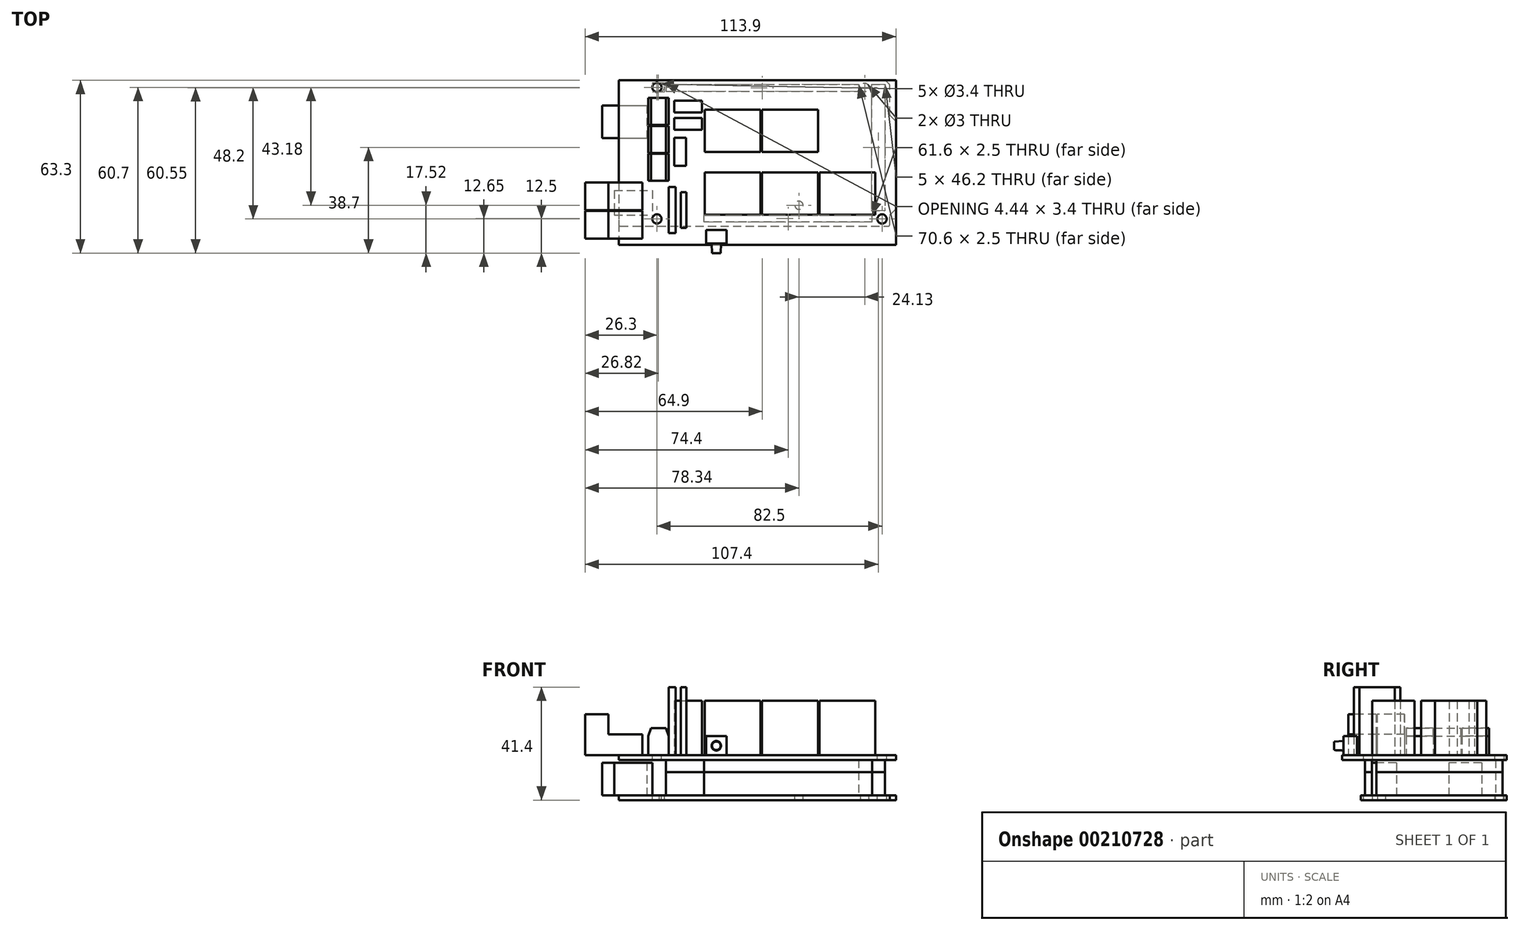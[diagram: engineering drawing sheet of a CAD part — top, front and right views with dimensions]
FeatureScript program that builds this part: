
annotation { "Feature Type Name" : "Feature", "Feature Type Description" : "" }
export const myFeature = defineFeature(function(context is Context, id is Id, definition is map)
    precondition{}
    {
        {
            var Q0;
            Q0=qCreatedBy(makeId("Top.planeOp"),FACE);
            var sketch = newSketch(context, id + "F0", { "sketchPlane" : qUnion([Q0])});
            skLineSegment(sketch, "E0.bottom", {"start": v(-50.8, 26.7) * mm, "end": v(50.8, 26.7) * mm, "construction": true});
            skLineSegment(sketch, "E0.top", {"start": v(-50.8, -26.7) * mm, "end": v(50.8, -26.7) * mm, "construction": true});
            skLineSegment(sketch, "E0.left", {"start": v(-50.8, 26.7) * mm, "end": v(-50.8, -26.7) * mm});
            skLineSegment(sketch, "E0.right", {"start": v(50.8, 26.7) * mm, "end": v(50.8, -26.7) * mm, "construction": true});
            skLineSegment(sketch, "E1", {"start": v(50.8, -26.7) * mm, "end": v(-50.8, 26.7) * mm, "construction": true});
            skLineSegment(sketch, "E2", {"start": v(-50.8, -26.7) * mm, "end": v(48.5, -26.7) * mm});
            skLineSegment(sketch, "E3", {"start": v(48.5, -26.7) * mm, "end": v(48.5, -22.7) * mm});
            skLineSegment(sketch, "E4", {"start": v(48.5, -22.7) * mm, "end": v(50.8, -20.4) * mm});
            skLineSegment(sketch, "E5", {"start": v(50.8, -20.4) * mm, "end": v(50.8, 11.6) * mm});
            skLineSegment(sketch, "E6", {"start": v(50.8, 11.6) * mm, "end": v(48.5, 13.9) * mm});
            skLineSegment(sketch, "E7", {"start": v(48.5, 13.9) * mm, "end": v(48.5, 25.1) * mm});
            skLineSegment(sketch, "E8", {"start": v(48.5, 25.1) * mm, "end": v(46.9, 26.7) * mm});
            skLineSegment(sketch, "E9", {"start": v(46.9, 26.7) * mm, "end": v(-50.8, 26.7) * mm});
            skSolve(sketch);
        }
        {
            var Q0;
            Q0=makeQuery(id+"F0.imprint","IMPRINT",FACE,{"disambiguationData":[TD([[makeQuery(id+"F0.imprint","IMPRINT",EDGE,{"derivedFrom":sQuery(id+"F0.wireOp",EDGE,"E0.left")}),1.0]])]});
            extrude(context, id + "F1", {"entities" : qUnion([Q0]), "depth" : 1.7 * mm});
        }
        {
            var Q0;
            Q0=makeQuery(id+"F1.opExtrude","CAP_FACE",FACE,{"disambiguationData":[OSD([sQuery(id+"F0.wireOp",EDGE,"E0.left"),sQuery(id+"F0.wireOp",EDGE,"E2"),sQuery(id+"F0.wireOp",EDGE,"E3"),sQuery(id+"F0.wireOp",EDGE,"E4"),sQuery(id+"F0.wireOp",EDGE,"E5"),sQuery(id+"F0.wireOp",EDGE,"E6"),sQuery(id+"F0.wireOp",EDGE,"E7"),sQuery(id+"F0.wireOp",EDGE,"E8"),sQuery(id+"F0.wireOp",EDGE,"E9")])],"isStart":false});
            var sketch = newSketch(context, id + "F2", { "sketchPlane" : qUnion([Q0])});
            skPoint(sketch, "E10", {"position": v(-35.56, 24.1) * mm});
            skPoint(sketch, "E11", {"position": v(39.37, 24.1) * mm});
            skPoint(sketch, "E12", {"position": v(15.24, -19.08) * mm});
            skPoint(sketch, "E13", {"position": v(-36.83, -24.16) * mm});
            skPoint(sketch, "E14", {"position": v(45.72, -24.16) * mm});
            skSolve(sketch);
        }
        {
            var Q0;
            Q0=sQuery(id+"F2.wireOp",VERTEX,"E10");
            var Q1;
            Q1=sQuery(id+"F2.wireOp",VERTEX,"E11");
            var Q2;
            Q2=sQuery(id+"F2.wireOp",VERTEX,"E12");
            var Q3;
            Q3=sQuery(id+"F2.wireOp",VERTEX,"E14");
            var Q4;
            Q4=sQuery(id+"F2.wireOp",VERTEX,"E13");
            var Q5;
            Q5=makeQuery(id+"F1.opExtrude","SWEPT_BODY",BODY,{"disambiguationData":[OSD([sQuery(id+"F0.wireOp",EDGE,"E0.left"),sQuery(id+"F0.wireOp",EDGE,"E2"),sQuery(id+"F0.wireOp",EDGE,"E3"),sQuery(id+"F0.wireOp",EDGE,"E4"),sQuery(id+"F0.wireOp",EDGE,"E5"),sQuery(id+"F0.wireOp",EDGE,"E6"),sQuery(id+"F0.wireOp",EDGE,"E7"),sQuery(id+"F0.wireOp",EDGE,"E8"),sQuery(id+"F0.wireOp",EDGE,"E9")])]});
            hole(context, id + "F3", {"style" : HoleStyle.SIMPLE, "endStyle" : HoleEndStyle.THROUGH, "holeDiameter" : 3 * mm, "locations" : qUnion([Q0, Q1, Q2, Q3, Q4]), "scope" : qUnion([Q5]), "isTappedThrough" : true});
        }
        {
            var Q0;
            Q0=makeQuery(id+"F1.opExtrude","SWEPT_EDGE",EDGE,{"disambiguationData":[OSD([sQuery(id+"F0.wireOp",EDGE,"E0.left"),sQuery(id+"F0.wireOp",EDGE,"E9")])]});
            var Q1;
            Q1=makeQuery(id+"F1.opExtrude","SWEPT_EDGE",EDGE,{"disambiguationData":[OSD([sQuery(id+"F0.wireOp",EDGE,"E0.left"),sQuery(id+"F0.wireOp",EDGE,"E2")])]});
            var Q2;
            Q2=makeQuery(id+"F1.opExtrude","SWEPT_EDGE",EDGE,{"disambiguationData":[OSD([sQuery(id+"F0.wireOp",EDGE,"E2"),sQuery(id+"F0.wireOp",EDGE,"E3")])]});
            var Q3;
            Q3=makeQuery(id+"F1.opExtrude","SWEPT_EDGE",EDGE,{"disambiguationData":[OSD([sQuery(id+"F0.wireOp",EDGE,"E3"),sQuery(id+"F0.wireOp",EDGE,"E4")])]});
            var Q4;
            Q4=makeQuery(id+"F1.opExtrude","SWEPT_EDGE",EDGE,{"disambiguationData":[OSD([sQuery(id+"F0.wireOp",EDGE,"E4"),sQuery(id+"F0.wireOp",EDGE,"E5")])]});
            var Q5;
            Q5=makeQuery(id+"F1.opExtrude","SWEPT_EDGE",EDGE,{"disambiguationData":[OSD([sQuery(id+"F0.wireOp",EDGE,"E5"),sQuery(id+"F0.wireOp",EDGE,"E6")])]});
            var Q6;
            Q6=makeQuery(id+"F1.opExtrude","SWEPT_EDGE",EDGE,{"disambiguationData":[OSD([sQuery(id+"F0.wireOp",EDGE,"E6"),sQuery(id+"F0.wireOp",EDGE,"E7")])]});
            var Q7;
            Q7=makeQuery(id+"F1.opExtrude","SWEPT_EDGE",EDGE,{"disambiguationData":[OSD([sQuery(id+"F0.wireOp",EDGE,"E7"),sQuery(id+"F0.wireOp",EDGE,"E8")])]});
            var Q8;
            Q8=makeQuery(id+"F1.opExtrude","SWEPT_EDGE",EDGE,{"disambiguationData":[OSD([sQuery(id+"F0.wireOp",EDGE,"E8"),sQuery(id+"F0.wireOp",EDGE,"E9")])]});
            fillet(context, id + "F4", {"entities" : qUnion([Q0, Q1, Q2, Q3, Q4, Q5, Q6, Q7, Q8]), "radius" : .5 * mm, "tangentPropagation" : true, "allowEdgeOverflow" : false});
        }
        {
            var Q0;
            Q0=makeQuery(id+"F1.opExtrude","CAP_FACE",FACE,{"disambiguationData":[OSD([sQuery(id+"F0.wireOp",EDGE,"E0.left"),sQuery(id+"F0.wireOp",EDGE,"E2"),sQuery(id+"F0.wireOp",EDGE,"E3"),sQuery(id+"F0.wireOp",EDGE,"E4"),sQuery(id+"F0.wireOp",EDGE,"E5"),sQuery(id+"F0.wireOp",EDGE,"E6"),sQuery(id+"F0.wireOp",EDGE,"E7"),sQuery(id+"F0.wireOp",EDGE,"E8"),sQuery(id+"F0.wireOp",EDGE,"E9")])],"isStart":false});
            var sketch = newSketch(context, id + "F5", { "sketchPlane" : qUnion([Q0])});
            skLineSegment(sketch, "E15.bottom", {"start": v(-52.4, -13.7) * mm, "end": v(-38.4, -13.7) * mm});
            skLineSegment(sketch, "E15.top", {"start": v(-52.4, -22.7) * mm, "end": v(-38.4, -22.7) * mm});
            skLineSegment(sketch, "E15.left", {"start": v(-52.4, -13.7) * mm, "end": v(-52.4, -22.7) * mm});
            skLineSegment(sketch, "E15.right", {"start": v(-38.4, -13.7) * mm, "end": v(-38.4, -22.7) * mm});
            skLineSegment(sketch, "E16.bottom", {"start": v(-56.9, 17.5) * mm, "end": v(-40.5, 17.5) * mm});
            skLineSegment(sketch, "E16.top", {"start": v(-56.9, 5.5) * mm, "end": v(-40.5, 5.5) * mm});
            skLineSegment(sketch, "E16.left", {"start": v(-56.9, 17.5) * mm, "end": v(-56.9, 5.5) * mm});
            skLineSegment(sketch, "E16.right", {"start": v(-40.5, 17.5) * mm, "end": v(-40.5, 5.5) * mm});
            skSolve(sketch);
        }
        {
            var Q0;
            {var subQ0=sQuery(id+"F5.wireOp",EDGE,"E16.left");Q0=makeQuery(id+"F5.imprint","IMPRINT",FACE,{"disambiguationData":[TD([[makeQuery(id+"F5.imprint","IMPRINT",EDGE,{"derivedFrom":subQ0}),1.0]])]});}
            var Q1;
            {var subQ0=sQuery(id+"F5.wireOp",EDGE,"E16.right");Q1=makeQuery(id+"F5.imprint","IMPRINT",FACE,{"disambiguationData":[TD([[makeQuery(id+"F5.imprint","IMPRINT",EDGE,{"derivedFrom":subQ0}),-1.0]])]});}
            var Q2;
            {var subQ0=sQuery(id+"F5.wireOp",EDGE,"E15.right");Q2=makeQuery(id+"F5.imprint","IMPRINT",FACE,{"disambiguationData":[TD([[makeQuery(id+"F5.imprint","IMPRINT",EDGE,{"derivedFrom":subQ0}),-1.0]])]});}
            var Q3;
            {var subQ0=sQuery(id+"F5.wireOp",EDGE,"E15.left");Q3=makeQuery(id+"F5.imprint","IMPRINT",FACE,{"disambiguationData":[TD([[makeQuery(id+"F5.imprint","IMPRINT",EDGE,{"derivedFrom":subQ0}),1.0]])]});}
            extrude(context, id + "F6", {"entities" : qUnion([Q0, Q1, Q2, Q3]), "depth" : 12 * mm});
        }
        {
            var Q0;
            Q0=makeQuery(id+"F1.opExtrude","CAP_FACE",FACE,{"disambiguationData":[OSD([sQuery(id+"F0.wireOp",EDGE,"E0.left"),sQuery(id+"F0.wireOp",EDGE,"E2"),sQuery(id+"F0.wireOp",EDGE,"E3"),sQuery(id+"F0.wireOp",EDGE,"E4"),sQuery(id+"F0.wireOp",EDGE,"E5"),sQuery(id+"F0.wireOp",EDGE,"E6"),sQuery(id+"F0.wireOp",EDGE,"E7"),sQuery(id+"F0.wireOp",EDGE,"E8"),sQuery(id+"F0.wireOp",EDGE,"E9")])],"isStart":false});
            var sketch = newSketch(context, id + "F7", { "sketchPlane" : qUnion([Q0])});
            skLineSegment(sketch, "E17.bottom", {"start": v(-33.5, 25.2) * mm, "end": v(37.1, 25.2) * mm});
            skLineSegment(sketch, "E17.top", {"start": v(-33.5, 22.7) * mm, "end": v(37.1, 22.7) * mm});
            skLineSegment(sketch, "E17.left", {"start": v(-33.5, 25.2) * mm, "end": v(-33.5, 22.7) * mm});
            skLineSegment(sketch, "E17.right", {"start": v(37.1, 25.2) * mm, "end": v(37.1, 22.7) * mm});
            skLineSegment(sketch, "E18.bottom", {"start": v(41.8, 25.2) * mm, "end": v(46.8, 25.2) * mm});
            skLineSegment(sketch, "E18.top", {"start": v(41.8, -21) * mm, "end": v(46.8, -21) * mm});
            skLineSegment(sketch, "E18.left", {"start": v(41.8, 25.2) * mm, "end": v(41.8, -21) * mm});
            skLineSegment(sketch, "E18.right", {"start": v(46.8, 25.2) * mm, "end": v(46.8, -21) * mm});
            skLineSegment(sketch, "E19.bottom", {"start": v(42.1, -25.2) * mm, "end": v(-19.5, -25.2) * mm});
            skLineSegment(sketch, "E19.top", {"start": v(42.1, -22.7) * mm, "end": v(-19.5, -22.7) * mm});
            skLineSegment(sketch, "E19.left", {"start": v(42.1, -25.2) * mm, "end": v(42.1, -22.7) * mm});
            skLineSegment(sketch, "E19.right", {"start": v(-19.5, -25.2) * mm, "end": v(-19.5, -22.7) * mm});
            skSolve(sketch);
        }
        {
            var Q0;
            Q0 = qSketchRegion(id + "F7", true);
            extrude(context, id + "F8", {"entities" : qUnion([Q0]), "operationType" : NewBodyOperationType.ADD, "depth" : 8.6 * mm});
        }
        {
            var Q0;
            Q0=makeQuery(id+"F8.opExtrude","CAP_FACE",FACE,{"disambiguationData":[OSD([sQuery(id+"F7.wireOp",EDGE,"E17.bottom"),sQuery(id+"F7.wireOp",EDGE,"E17.top"),sQuery(id+"F7.wireOp",EDGE,"E17.left"),sQuery(id+"F7.wireOp",EDGE,"E17.right")])],"isStart":false});
            var sketch = newSketch(context, id + "F9", { "sketchPlane" : qUnion([Q0])});
            skLineSegment(sketch, "E20.1.0", {"start": v(41.8, 25.2) * mm, "end": v(41.8, -21) * mm});
            skLineSegment(sketch, "E20.1.1", {"start": v(41.8, -21) * mm, "end": v(46.8, -21) * mm});
            skLineSegment(sketch, "E20.1.2", {"start": v(46.8, -21) * mm, "end": v(46.8, 25.2) * mm});
            skLineSegment(sketch, "E20.1.3", {"start": v(46.8, 25.2) * mm, "end": v(41.8, 25.2) * mm});
            skLineSegment(sketch, "E20.2.0", {"start": v(42.1, -25.2) * mm, "end": v(42.1, -22.7) * mm});
            skLineSegment(sketch, "E20.2.1", {"start": v(42.1, -22.7) * mm, "end": v(-19.5, -22.7) * mm});
            skLineSegment(sketch, "E20.2.2", {"start": v(-19.5, -22.7) * mm, "end": v(-19.5, -25.2) * mm});
            skLineSegment(sketch, "E20.2.3", {"start": v(-19.5, -25.2) * mm, "end": v(42.1, -25.2) * mm});
            skLineSegment(sketch, "E21.0", {"start": v(-33.5, 22.7) * mm, "end": v(37.1, 22.7) * mm});
            skLineSegment(sketch, "E22.0", {"start": v(-33.5, 25.2) * mm, "end": v(-33.5, 22.7) * mm});
            skLineSegment(sketch, "E22.1", {"start": v(-33.5, 25.2) * mm, "end": v(37.1, 25.2) * mm});
            skLineSegment(sketch, "E22.2", {"start": v(37.1, 25.2) * mm, "end": v(37.1, 22.7) * mm});
            skSolve(sketch);
        }
        {
            var Q0;
            Q0 = qSketchRegion(id + "F9", true);
            extrude(context, id + "F10", {"entities" : qUnion([Q0]), "depth" : 4.4 * mm});
        }
        {
            var Q0;
            Q0=makeQuery(id+"F10.opExtrude","CAP_FACE",FACE,{"disambiguationData":[OSD([sQuery(id+"F9.wireOp",EDGE,"E21.0"),sQuery(id+"F9.wireOp",EDGE,"E22.0"),sQuery(id+"F9.wireOp",EDGE,"E22.1"),sQuery(id+"F9.wireOp",EDGE,"E22.2")])],"isStart":false});
            var sketch = newSketch(context, id + "F11", { "sketchPlane" : qUnion([Q0])});
            skLineSegment(sketch, "E23", {"start": v(50.8, 26.7) * mm, "end": v(-50.8, 26.7) * mm});
            skLineSegment(sketch, "E24", {"start": v(-50.8, 26.7) * mm, "end": v(-50.8, -33.6) * mm});
            skLineSegment(sketch, "E25", {"start": v(-50.8, -33.6) * mm, "end": v(50.8, -33.6) * mm});
            skLineSegment(sketch, "E26", {"start": v(50.8, -33.6) * mm, "end": v(50.8, 26.7) * mm});
            skSolve(sketch);
        }
        {
            var Q0;
            Q0 = qSketchRegion(id + "F11", true);
            extrude(context, id + "F12", {"entities" : qUnion([Q0]), "operationType" : NewBodyOperationType.ADD, "depth" : 1.7 * mm});
        }
        {
            var Q0;
            Q0=makeQuery(id+"F12.opExtrude","CAP_FACE",FACE,{"disambiguationData":[OSD([sQuery(id+"F11.wireOp",EDGE,"E23"),sQuery(id+"F11.wireOp",EDGE,"E24"),sQuery(id+"F11.wireOp",EDGE,"E25"),sQuery(id+"F11.wireOp",EDGE,"E26")])],"isStart":false});
            var sketch = newSketch(context, id + "F13", { "sketchPlane" : qUnion([Q0])});
            skPoint(sketch, "E27", {"position": v(-36.8, 24.1) * mm});
            skPoint(sketch, "E28", {"position": v(-36.8, -24.1) * mm});
            skPoint(sketch, "E29", {"position": v(45.7, -24.1) * mm});
            skSolve(sketch);
        }
        {
            var Q0;
            Q0=sQuery(id+"F13.wireOp",VERTEX,"E28");
            var Q1;
            Q1=sQuery(id+"F13.wireOp",VERTEX,"E27");
            var Q2;
            Q2=sQuery(id+"F13.wireOp",VERTEX,"E29");
            var Q3;
            Q3=makeQuery(id+"F1.opExtrude","SWEPT_BODY",BODY,{"disambiguationData":[OSD([sQuery(id+"F0.wireOp",EDGE,"E0.left"),sQuery(id+"F0.wireOp",EDGE,"E2"),sQuery(id+"F0.wireOp",EDGE,"E3"),sQuery(id+"F0.wireOp",EDGE,"E4"),sQuery(id+"F0.wireOp",EDGE,"E5"),sQuery(id+"F0.wireOp",EDGE,"E6"),sQuery(id+"F0.wireOp",EDGE,"E7"),sQuery(id+"F0.wireOp",EDGE,"E8"),sQuery(id+"F0.wireOp",EDGE,"E9")])]});
            var Q4;
            Q4=makeQuery(id+"F10.opExtrude","SWEPT_BODY",BODY,{"disambiguationData":[OSD([sQuery(id+"F9.wireOp",EDGE,"E20.1.0"),sQuery(id+"F9.wireOp",EDGE,"E20.1.1"),sQuery(id+"F9.wireOp",EDGE,"E20.1.2"),sQuery(id+"F9.wireOp",EDGE,"E20.1.3")])]});
            hole(context, id + "F14", {"style" : HoleStyle.SIMPLE, "endStyle" : HoleEndStyle.THROUGH, "holeDiameter" : 3.4 * mm, "locations" : qUnion([Q0, Q1, Q2]), "scope" : qUnion([Q3, Q4]), "isTappedThrough" : true});
        }
        {
            var Q0;
            Q0=makeQuery(id+"F12.opExtrude","CAP_FACE",FACE,{"disambiguationData":[OSD([sQuery(id+"F11.wireOp",EDGE,"E23"),sQuery(id+"F11.wireOp",EDGE,"E24"),sQuery(id+"F11.wireOp",EDGE,"E25"),sQuery(id+"F11.wireOp",EDGE,"E26")])],"isStart":false});
            var sketch = newSketch(context, id + "F15", { "sketchPlane" : qUnion([Q0])});
            skLineSegment(sketch, "E30.bottom", {"start": v(-42.1, -21.15) * mm, "end": v(-63.1, -21.15) * mm});
            skLineSegment(sketch, "E30.top", {"start": v(-42.1, -31.3) * mm, "end": v(-63.1, -31.3) * mm});
            skLineSegment(sketch, "E30.left", {"start": v(-42.1, -21.15) * mm, "end": v(-42.1, -31.3) * mm});
            skLineSegment(sketch, "E30.right", {"start": v(-63.1, -21.15) * mm, "end": v(-63.1, -31.3) * mm});
            skLineSegment(sketch, "E31.bottom", {"start": v(-42.1, -10.7) * mm, "end": v(-63.1, -10.7) * mm});
            skLineSegment(sketch, "E31.top", {"start": v(-42.1, -20.85) * mm, "end": v(-63.1, -20.85) * mm});
            skLineSegment(sketch, "E31.left", {"start": v(-42.1, -10.7) * mm, "end": v(-42.1, -20.85) * mm});
            skLineSegment(sketch, "E31.right", {"start": v(-63.1, -10.7) * mm, "end": v(-63.1, -20.85) * mm});
            skSolve(sketch);
        }
        {
            var Q0;
            Q0 = qSketchRegion(id + "F15", true);
            extrude(context, id + "F16", {"entities" : qUnion([Q0]), "depth" : 15 * mm});
        }
        {
            var Q0;
            Q0=makeQuery(id+"F16.opExtrude","SWEPT_FACE",FACE,{"disambiguationData":[OSD([sQuery(id+"F15.wireOp",EDGE,"E30.top")])]});
            var sketch = newSketch(context, id + "F17", { "sketchPlane" : qUnion([Q0])});
            skLineSegment(sketch, "E32.bottom", {"start": v(-54.6, 31.4) * mm, "end": v(-42.1, 31.4) * mm});
            skLineSegment(sketch, "E32.top", {"start": v(-54.6, 24.1) * mm, "end": v(-42.1, 24.1) * mm});
            skLineSegment(sketch, "E32.left", {"start": v(-54.6, 31.4) * mm, "end": v(-54.6, 24.1) * mm});
            skLineSegment(sketch, "E32.right", {"start": v(-42.1, 31.4) * mm, "end": v(-42.1, 24.1) * mm});
            skSolve(sketch);
        }
        {
            var Q0;
            Q0 = qSketchRegion(id + "F17", true);
            var Q1;
            Q1=makeQuery(id+"F16.opExtrude","SWEPT_FACE",FACE,{"disambiguationData":[OSD([sQuery(id+"F15.wireOp",EDGE,"E31.bottom")])]});
            extrude(context, id + "F18", {"entities" : qUnion([Q0]), "operationType" : NewBodyOperationType.REMOVE, "endBound" : BoundingType.UP_TO_SURFACE, "oppositeDirection" : true, "endBoundEntityFace" : qUnion([Q1]), "depth" : 25 * mm});
        }
        {
            var Q0;
            Q0=makeQuery(id+"F12.opExtrude","CAP_FACE",FACE,{"disambiguationData":[OSD([sQuery(id+"F11.wireOp",EDGE,"E23"),sQuery(id+"F11.wireOp",EDGE,"E24"),sQuery(id+"F11.wireOp",EDGE,"E25"),sQuery(id+"F11.wireOp",EDGE,"E26")])],"isStart":false});
            var sketch = newSketch(context, id + "F19", { "sketchPlane" : qUnion([Q0])});
            skLineSegment(sketch, "E33.bottom", {"start": v(-40, 20.2) * mm, "end": v(-32.5, 20.2) * mm});
            skLineSegment(sketch, "E33.top", {"start": v(-40, 10.3) * mm, "end": v(-32.5, 10.3) * mm});
            skLineSegment(sketch, "E33.left", {"start": v(-40, 20.2) * mm, "end": v(-40, 10.3) * mm});
            skLineSegment(sketch, "E33.right", {"start": v(-32.5, 20.2) * mm, "end": v(-32.5, 10.3) * mm});
            skLineSegment(sketch, "E34.bottom", {"start": v(-40, 10) * mm, "end": v(-32.5, 10) * mm});
            skLineSegment(sketch, "E34.top", {"start": v(-40, 0.1) * mm, "end": v(-32.5, 0.1) * mm});
            skLineSegment(sketch, "E34.left", {"start": v(-40, 10) * mm, "end": v(-40, 0.1) * mm});
            skLineSegment(sketch, "E34.right", {"start": v(-32.5, 10) * mm, "end": v(-32.5, 0.1) * mm});
            skLineSegment(sketch, "E35.bottom", {"start": v(-40, -0.2) * mm, "end": v(-32.5, -0.2) * mm});
            skLineSegment(sketch, "E35.top", {"start": v(-40, -10.1) * mm, "end": v(-32.5, -10.1) * mm});
            skLineSegment(sketch, "E35.left", {"start": v(-40, -0.2) * mm, "end": v(-40, -10.1) * mm});
            skLineSegment(sketch, "E35.right", {"start": v(-32.5, -0.2) * mm, "end": v(-32.5, -10.1) * mm});
            skSolve(sketch);
        }
        {
            var Q0;
            Q0 = qSketchRegion(id + "F19", true);
            extrude(context, id + "F20", {"entities" : qUnion([Q0]), "depth" : 10 * mm});
        }
        {
            var Q0;
            Q0=makeQuery(id+"F20.opExtrude","CAP_EDGE",EDGE,{"disambiguationData":[OSD([sQuery(id+"F19.wireOp",EDGE,"E33.left")])],"isStart":false});
            var Q1;
            Q1=makeQuery(id+"F20.opExtrude","CAP_EDGE",EDGE,{"disambiguationData":[OSD([sQuery(id+"F19.wireOp",EDGE,"E34.left")])],"isStart":false});
            var Q2;
            Q2=makeQuery(id+"F20.opExtrude","CAP_EDGE",EDGE,{"disambiguationData":[OSD([sQuery(id+"F19.wireOp",EDGE,"E35.left")])],"isStart":false});
            var Q3;
            Q3=makeQuery(id+"F20.opExtrude","CAP_EDGE",EDGE,{"disambiguationData":[OSD([sQuery(id+"F19.wireOp",EDGE,"E35.right")])],"isStart":false});
            var Q4;
            Q4=makeQuery(id+"F20.opExtrude","CAP_EDGE",EDGE,{"disambiguationData":[OSD([sQuery(id+"F19.wireOp",EDGE,"E34.right")])],"isStart":false});
            var Q5;
            Q5=makeQuery(id+"F20.opExtrude","CAP_EDGE",EDGE,{"disambiguationData":[OSD([sQuery(id+"F19.wireOp",EDGE,"E33.right")])],"isStart":false});
            chamfer(context, id + "F21", {"entities" : qUnion([Q0, Q1, Q2, Q3, Q4, Q5]), "chamferType" : ChamferType.TWO_OFFSETS, "width1" : 1 * mm, "oppositeDirection" : false, "width2" : 3 * mm, "tangentPropagation" : true});
        }
        {
            var Q0;
            Q0=makeQuery(id+"F12.opExtrude","CAP_FACE",FACE,{"disambiguationData":[OSD([sQuery(id+"F11.wireOp",EDGE,"E23"),sQuery(id+"F11.wireOp",EDGE,"E24"),sQuery(id+"F11.wireOp",EDGE,"E25"),sQuery(id+"F11.wireOp",EDGE,"E26")])],"isStart":false});
            var sketch = newSketch(context, id + "F22", { "sketchPlane" : qUnion([Q0])});
            skLineSegment(sketch, "E36.bottom", {"start": v(-30.5, 19.2) * mm, "end": v(-20.3, 19.2) * mm});
            skLineSegment(sketch, "E36.top", {"start": v(-30.5, 14.9) * mm, "end": v(-20.3, 14.9) * mm});
            skLineSegment(sketch, "E36.left", {"start": v(-30.5, 19.2) * mm, "end": v(-30.5, 14.9) * mm});
            skLineSegment(sketch, "E36.right", {"start": v(-20.3, 19.2) * mm, "end": v(-20.3, 14.9) * mm});
            skLineSegment(sketch, "E37.bottom", {"start": v(-30.5, 12.9) * mm, "end": v(-20.3, 12.9) * mm});
            skLineSegment(sketch, "E37.top", {"start": v(-30.5, 8.6) * mm, "end": v(-20.3, 8.6) * mm});
            skLineSegment(sketch, "E37.left", {"start": v(-30.5, 12.9) * mm, "end": v(-30.5, 8.6) * mm});
            skLineSegment(sketch, "E37.right", {"start": v(-20.3, 12.9) * mm, "end": v(-20.3, 8.6) * mm});
            skLineSegment(sketch, "E38.bottom", {"start": v(-30.5, 5.6) * mm, "end": v(-26.2, 5.6) * mm});
            skLineSegment(sketch, "E38.top", {"start": v(-30.5, -4.6) * mm, "end": v(-26.2, -4.6) * mm});
            skLineSegment(sketch, "E38.left", {"start": v(-30.5, 5.6) * mm, "end": v(-30.5, -4.6) * mm});
            skLineSegment(sketch, "E38.right", {"start": v(-26.2, 5.6) * mm, "end": v(-26.2, -4.6) * mm});
            skLineSegment(sketch, "E39.bottom", {"start": v(-19.3, 15.9) * mm, "end": v(1.2, 15.9) * mm});
            skLineSegment(sketch, "E39.top", {"start": v(-19.3, 0.4) * mm, "end": v(1.2, 0.4) * mm});
            skLineSegment(sketch, "E39.left", {"start": v(-19.3, 15.9) * mm, "end": v(-19.3, 0.4) * mm});
            skLineSegment(sketch, "E39.right", {"start": v(1.2, 15.9) * mm, "end": v(1.2, 0.4) * mm});
            skLineSegment(sketch, "E40.bottom", {"start": v(1.7, 15.9) * mm, "end": v(22.2, 15.9) * mm});
            skLineSegment(sketch, "E40.top", {"start": v(1.7, 0.4) * mm, "end": v(22.2, 0.4) * mm});
            skLineSegment(sketch, "E40.left", {"start": v(1.7, 15.9) * mm, "end": v(1.7, 0.4) * mm});
            skLineSegment(sketch, "E40.right", {"start": v(22.2, 15.9) * mm, "end": v(22.2, 0.4) * mm});
            skLineSegment(sketch, "E41.bottom", {"start": v(-19.3, -7.1) * mm, "end": v(1.2, -7.1) * mm});
            skLineSegment(sketch, "E41.top", {"start": v(-19.3, -22.6) * mm, "end": v(1.2, -22.6) * mm});
            skLineSegment(sketch, "E41.left", {"start": v(-19.3, -7.1) * mm, "end": v(-19.3, -22.6) * mm});
            skLineSegment(sketch, "E41.right", {"start": v(1.2, -7.1) * mm, "end": v(1.2, -22.6) * mm});
            skLineSegment(sketch, "E42.bottom", {"start": v(1.7, -7.1) * mm, "end": v(22.2, -7.1) * mm});
            skLineSegment(sketch, "E42.top", {"start": v(1.7, -22.6) * mm, "end": v(22.2, -22.6) * mm});
            skLineSegment(sketch, "E42.left", {"start": v(1.7, -7.1) * mm, "end": v(1.7, -22.6) * mm});
            skLineSegment(sketch, "E42.right", {"start": v(22.2, -7.1) * mm, "end": v(22.2, -22.6) * mm});
            skLineSegment(sketch, "E43.bottom", {"start": v(22.7, -7.1) * mm, "end": v(43.2, -7.1) * mm});
            skLineSegment(sketch, "E43.top", {"start": v(22.7, -22.6) * mm, "end": v(43.2, -22.6) * mm});
            skLineSegment(sketch, "E43.left", {"start": v(22.7, -7.1) * mm, "end": v(22.7, -22.6) * mm});
            skLineSegment(sketch, "E43.right", {"start": v(43.2, -7.1) * mm, "end": v(43.2, -22.6) * mm});
            skSolve(sketch);
        }
        {
            var Q0;
            Q0 = qSketchRegion(id + "F22", true);
            extrude(context, id + "F23", {"entities" : qUnion([Q0]), "operationType" : NewBodyOperationType.ADD, "depth" : 20 * mm});
        }
        {
            var Q0;
            Q0=makeQuery(id+"F12.opExtrude","CAP_FACE",FACE,{"disambiguationData":[OSD([sQuery(id+"F11.wireOp",EDGE,"E23"),sQuery(id+"F11.wireOp",EDGE,"E24"),sQuery(id+"F11.wireOp",EDGE,"E25"),sQuery(id+"F11.wireOp",EDGE,"E26")])],"isStart":false});
            var sketch = newSketch(context, id + "F24", { "sketchPlane" : qUnion([Q0])});
            skLineSegment(sketch, "E44.bottom", {"start": v(-32.5, -12.33) * mm, "end": v(-30, -12.33) * mm});
            skLineSegment(sketch, "E44.top", {"start": v(-32.5, -29.33) * mm, "end": v(-30, -29.33) * mm});
            skLineSegment(sketch, "E44.left", {"start": v(-32.5, -12.33) * mm, "end": v(-32.5, -29.33) * mm});
            skLineSegment(sketch, "E44.right", {"start": v(-30, -12.33) * mm, "end": v(-30, -29.33) * mm});
            skLineSegment(sketch, "E45.bottom", {"start": v(-28, -14.33) * mm, "end": v(-26, -14.33) * mm});
            skLineSegment(sketch, "E45.top", {"start": v(-28, -27.33) * mm, "end": v(-26, -27.33) * mm});
            skLineSegment(sketch, "E45.left", {"start": v(-28, -14.33) * mm, "end": v(-28, -27.33) * mm});
            skLineSegment(sketch, "E45.right", {"start": v(-26, -14.33) * mm, "end": v(-26, -27.33) * mm});
            skLineSegment(sketch, "E46", {"start": v(-30, -20.83) * mm, "end": v(-28, -20.83) * mm});
            skSolve(sketch);
        }
        {
            var Q0;
            Q0 = qSketchRegion(id + "F24", true);
            extrude(context, id + "F25", {"entities" : qUnion([Q0]), "depth" : 25 * mm});
        }
        {
            var Q0;
            Q0=makeQuery(id+"F12.opExtrude","CAP_FACE",FACE,{"disambiguationData":[OSD([sQuery(id+"F11.wireOp",EDGE,"E23"),sQuery(id+"F11.wireOp",EDGE,"E24"),sQuery(id+"F11.wireOp",EDGE,"E25"),sQuery(id+"F11.wireOp",EDGE,"E26")])],"isStart":false});
            var sketch = newSketch(context, id + "F26", { "sketchPlane" : qUnion([Q0])});
            skLineSegment(sketch, "E47.bottom", {"start": v(-18.8, -28.1) * mm, "end": v(-11.3, -28.1) * mm});
            skLineSegment(sketch, "E47.top", {"start": v(-18.8, -33.1) * mm, "end": v(-11.3, -33.1) * mm});
            skLineSegment(sketch, "E47.left", {"start": v(-18.8, -28.1) * mm, "end": v(-18.8, -33.1) * mm});
            skLineSegment(sketch, "E47.right", {"start": v(-11.3, -28.1) * mm, "end": v(-11.3, -33.1) * mm});
            skSolve(sketch);
        }
        {
            var Q0;
            Q0 = qSketchRegion(id + "F26", true);
            extrude(context, id + "F27", {"entities" : qUnion([Q0]), "operationType" : NewBodyOperationType.ADD, "depth" : 7 * mm});
        }
        {
            var Q0;
            Q0=makeQuery(id+"F27.opExtrude","SWEPT_FACE",FACE,{"disambiguationData":[OSD([sQuery(id+"F26.wireOp",EDGE,"E47.top")])]});
            var sketch = newSketch(context, id + "F28", { "sketchPlane" : qUnion([Q0])});
            skCircle(sketch, "E48", {"center": v(-15.05, 19.9) * mm, "radius": 1.75 * mm});
            skLineSegment(sketch, "E49", {"start": v(-18.8, 23.4) * mm, "end": v(-11.3, 16.4) * mm, "construction": true});
            skSolve(sketch);
        }
        {
            var Q0;
            Q0=makeQuery(id+"F28.imprint","IMPRINT",FACE,{"disambiguationData":[TD([[makeQuery(id+"F28.imprint","IMPRINT",EDGE,{"derivedFrom":sQuery(id+"F28.wireOp",EDGE,"E48")}),1.0]])]});
            var Q1;
            Q1=sQuery(id+"F28.wireOp",EDGE,"E48");
            extrude(context, id + "F29", {"entities" : qUnion([Q0]), "operationType" : NewBodyOperationType.ADD, "surfaceEntities" : qUnion([Q1]), "depth" : 3.5 * mm, "hasDraft" : true, "draftAngle" : 3 * degree, "draftPullDirection" : true});
        }
    });
